# Revit family: Shower_Set-DXV-Randall-D35102780_Series
name_source: partatom
category: Plumbing Fixtures
revit_build: Autodesk Revit 2014 (Build: 20130308_1515(x64)
units: mm (PartAtom-declared; Revit-internal decimal feet)

## types (4) — shared parameters
Assembly Code = D2010710
CW Connection = Yes
CWFU = 3
CalGreen Compliant = Yes
Cold Water Connection Diameter = 1"
Cold Water Connection Radius = 1/2"
Default Elevation = 55 31/32"
Description = Randall Personal Shower Set with Hand Shower
Flow Rate = 2.0 GPM (7.6 L/min)
HW Connection = Yes
HWFU = 3
Height = 26 1/4"
Hot Water Connection Diameter = 1"
Hot Water Connection Radius = 1/2"
Installation Type = Wall Mounted
Length = 9 15/16"
Manufacturer = DXV
Price = Prices may vary. Please consult Manufacturer Representative for most up-to-date price list.
Product Documentation Link = https://dxv01.blob.core.windows.net
Product Page URL = https://www.dxv.com
Tempered Water Connection Diameter = 1/2"
Tempered Water Connection Radius = 1/4"
URL = https://www.dxv.com
Vent Connection = No
WFU = 4
Warranty Documentation Link = https://www.dxv.com
Waste Connection = No
Width = 7 13/16"

## per-type parameters (varying)
| type | Fnish | Material |
| D35102780.100 | Metal-DXV-100-Polished Chrome | Metal-DXV-100-Polished Chrome |
| D35102780.144 | Metal-DXV-144-Brushed Nickel | Metal-DXV-144-Brushed Nickel |
| D35102780.150 | Metal-DXV-150-Platinum Nickel | Metal-DXV-150-Platinum Nickel |
| D35102780.427 | Metal-DXV-427-Satin Brass | Metal-DXV-427-Satin Brass |

note: column(s) folded — value = type name in every type: Model

## geometry (parser evidence)
native form markers: Sweep x1
no freeform markers — native parametric forms only
